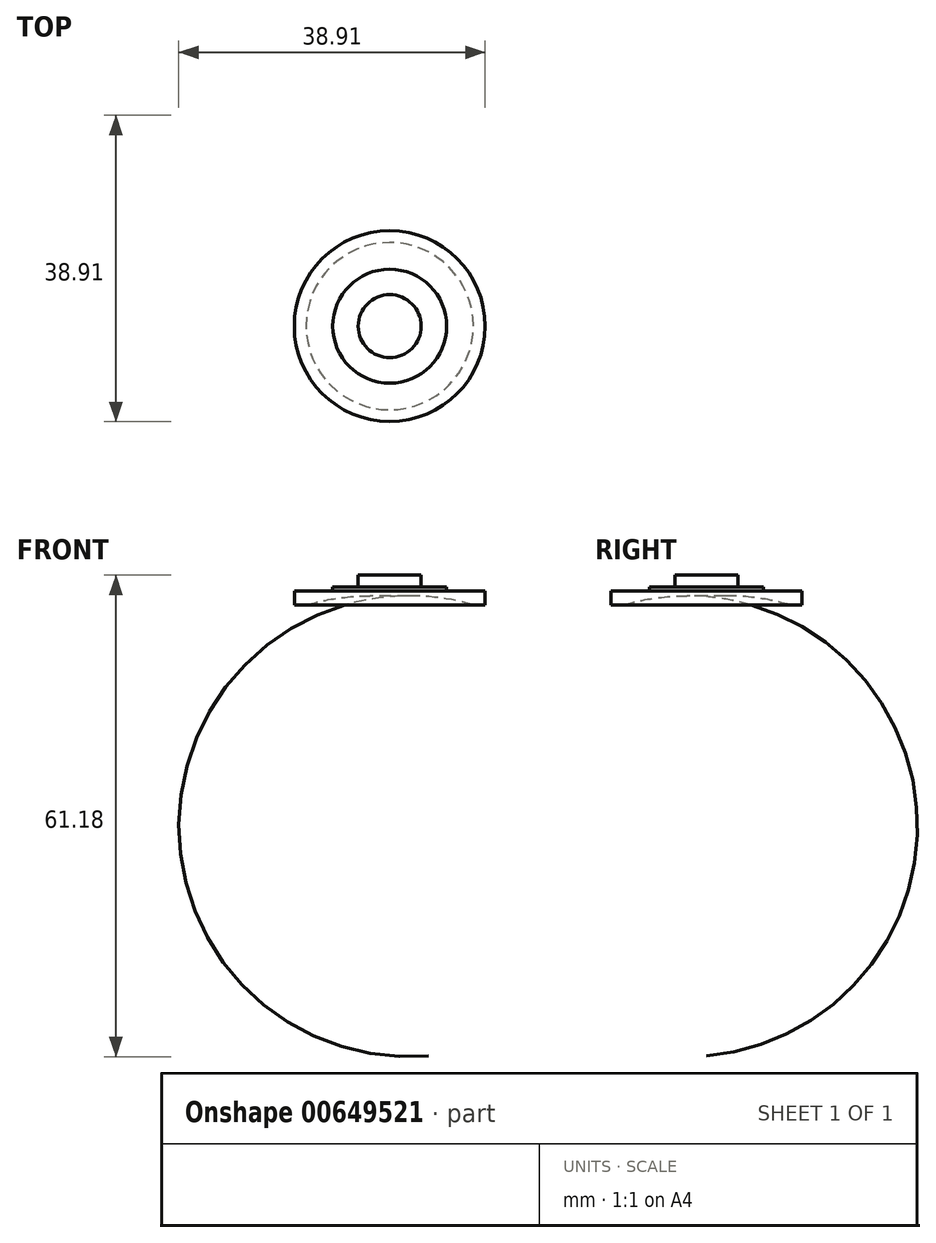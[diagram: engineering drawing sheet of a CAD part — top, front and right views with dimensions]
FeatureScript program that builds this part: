
annotation { "Feature Type Name" : "Feature", "Feature Type Description" : "" }
export const myFeature = defineFeature(function(context is Context, id is Id, definition is map)
    precondition{}
    {
        {
            var Q0;
            Q0=qCreatedBy(makeId("Front.planeOp"),FACE);
            var sketch = newSketch(context, id + "F0", { "sketchPlane" : qUnion([Q0])});
            skLineSegment(sketch, "E0", {"start": v(-4, 6.12) * mm, "end": v(-7.24, 6.12) * mm});
            skLineSegment(sketch, "E1", {"start": v(-7.24, 6.12) * mm, "end": v(-7.24, 5.62) * mm});
            skLineSegment(sketch, "E2", {"start": v(-7.24, 5.62) * mm, "end": v(-12.12, 5.62) * mm});
            skLineSegment(sketch, "E3", {"start": v(-12.12, 5.62) * mm, "end": v(-12.12, 3.82) * mm});
            skLineSegment(sketch, "E4", {"start": v(-4, 6.12) * mm, "end": v(-4, 7.62) * mm});
            skLineSegment(sketch, "E5", {"start": v(-4, 7.62) * mm, "end": v(0, 7.62) * mm});
            skLineSegment(sketch, "E6", {"start": v(-12.12, 3.82) * mm, "end": v(-10.62, 3.82) * mm});
            skLineSegment(sketch, "E7", {"start": v(0, 7.62) * mm, "end": v(0, 4.87) * mm});
            skArc(sketch, "E8", {"start": v(0, 4.87) * mm, "mid": v(-5.36, 4.84) * mm, "end": v(-10.62, 3.82) * mm});
            skSolve(sketch);
        }
        {
            var Q0;
            Q0=makeQuery(id+"F0.imprint","IMPRINT",FACE,{"disambiguationData":[TD([[makeQuery(id+"F0.imprint","IMPRINT",EDGE,{"derivedFrom":sQuery(id+"F0.wireOp",EDGE,"E0")}),1.0]])]});
            var Q1;
            Q1=sQuery(id+"F0.wireOp",EDGE,"E7");
            revolve(context, id + "F1", {"entities" : qUnion([Q0]), "axis" : qUnion([Q1]), "revolveType" : RevolveType.FULL});
        }
    });
